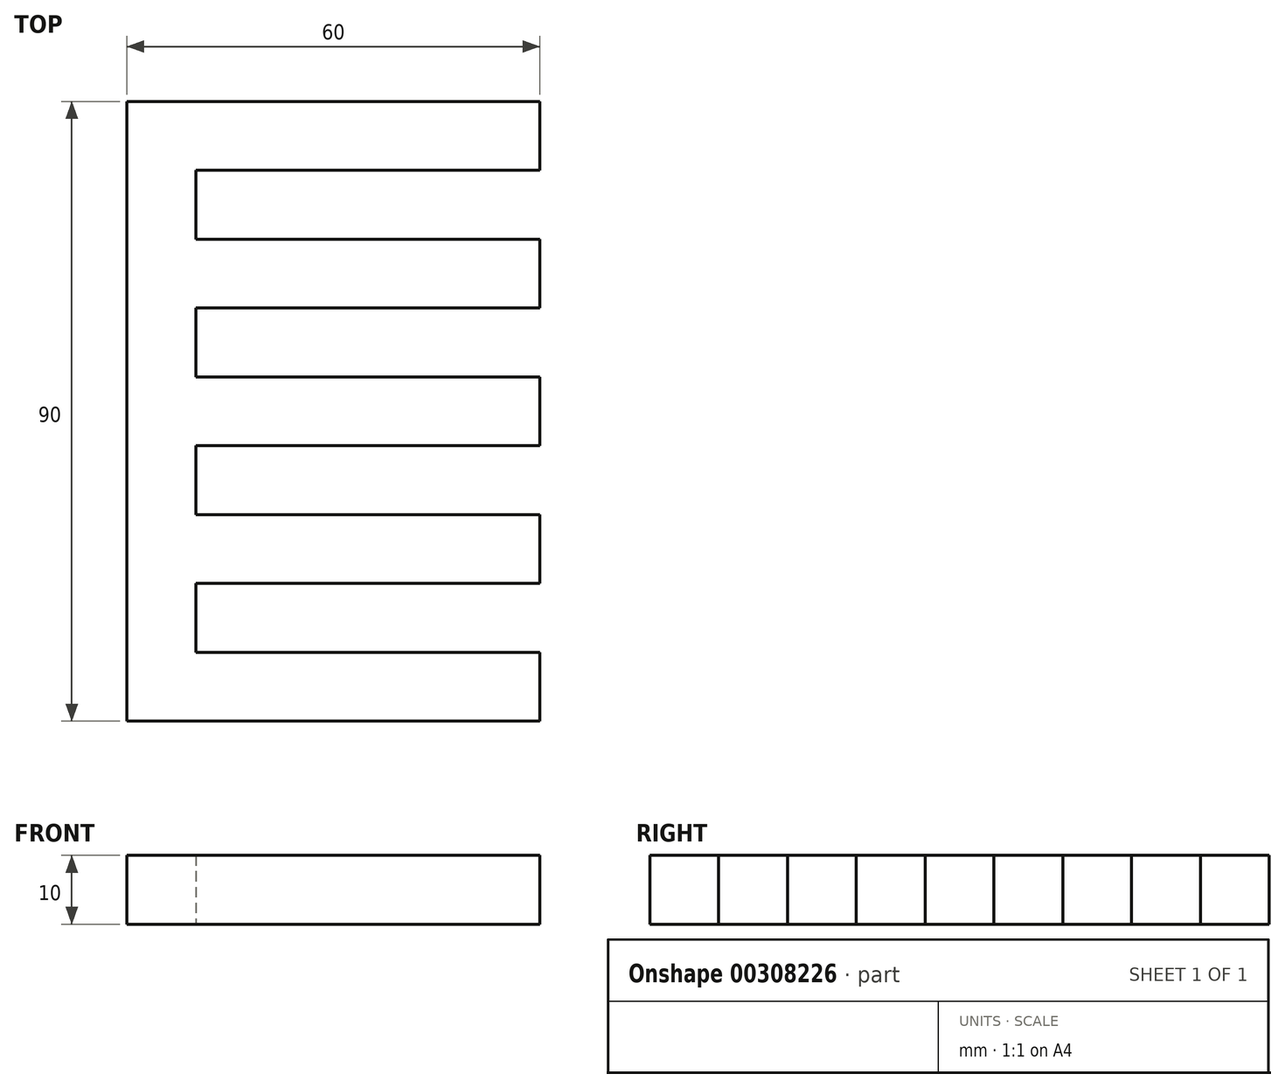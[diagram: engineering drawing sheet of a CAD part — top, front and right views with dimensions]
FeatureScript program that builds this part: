
annotation { "Feature Type Name" : "Feature", "Feature Type Description" : "" }
export const myFeature = defineFeature(function(context is Context, id is Id, definition is map)
    precondition{}
    {
        {
            var Q0;
            Q0=qCreatedBy(makeId("Top.planeOp"),FACE);
            var sketch = newSketch(context, id + "F0", { "sketchPlane" : qUnion([Q0])});
            skLineSegment(sketch, "E0", {"start": v(-20.13, 24.08) * mm, "end": v(39.87, 24.08) * mm});
            skLineSegment(sketch, "E1", {"start": v(39.87, 24.08) * mm, "end": v(39.87, 14.08) * mm});
            skLineSegment(sketch, "E2", {"start": v(39.87, 14.08) * mm, "end": v(-10.13, 14.08) * mm});
            skLineSegment(sketch, "E3", {"start": v(-10.13, 14.08) * mm, "end": v(-10.13, 4.08) * mm});
            skLineSegment(sketch, "E4", {"start": v(-10.13, 4.08) * mm, "end": v(39.87, 4.08) * mm});
            skLineSegment(sketch, "E5", {"start": v(39.87, 4.08) * mm, "end": v(39.87, -5.92) * mm});
            skLineSegment(sketch, "E6", {"start": v(39.87, -5.92) * mm, "end": v(-10.13, -5.92) * mm});
            skLineSegment(sketch, "E7", {"start": v(-10.13, -5.92) * mm, "end": v(-10.13, -15.92) * mm});
            skLineSegment(sketch, "E8", {"start": v(-10.13, -15.92) * mm, "end": v(39.87, -15.92) * mm});
            skLineSegment(sketch, "E9", {"start": v(39.87, -15.92) * mm, "end": v(39.87, -25.92) * mm});
            skLineSegment(sketch, "E10", {"start": v(39.87, -25.92) * mm, "end": v(-10.13, -25.92) * mm});
            skLineSegment(sketch, "E11", {"start": v(-10.13, -25.92) * mm, "end": v(-10.13, -35.92) * mm});
            skLineSegment(sketch, "E12", {"start": v(-10.13, -35.92) * mm, "end": v(39.87, -35.92) * mm});
            skLineSegment(sketch, "E13", {"start": v(39.87, -35.92) * mm, "end": v(39.87, -45.92) * mm});
            skLineSegment(sketch, "E14", {"start": v(39.87, -45.92) * mm, "end": v(-10.13, -45.92) * mm});
            skLineSegment(sketch, "E15", {"start": v(-10.13, -45.92) * mm, "end": v(-10.13, -55.92) * mm});
            skLineSegment(sketch, "E16", {"start": v(-10.13, -55.92) * mm, "end": v(39.87, -55.92) * mm});
            skLineSegment(sketch, "E17", {"start": v(39.87, -55.92) * mm, "end": v(39.87, -65.92) * mm});
            skLineSegment(sketch, "E18", {"start": v(39.87, -65.92) * mm, "end": v(-20.13, -65.92) * mm});
            skLineSegment(sketch, "E19", {"start": v(-20.13, -65.92) * mm, "end": v(-20.13, 24.08) * mm});
            skSolve(sketch);
        }
        {
            var Q0;
            Q0=makeQuery(id+"F0.imprint","IMPRINT",FACE,{"disambiguationData":[TD([[makeQuery(id+"F0.imprint","IMPRINT",EDGE,{"derivedFrom":sQuery(id+"F0.wireOp",EDGE,"E0")}),-1.0]])]});
            extrude(context, id + "F1", {"entities" : qUnion([Q0]), "depth" : 10 * mm});
        }
    });
